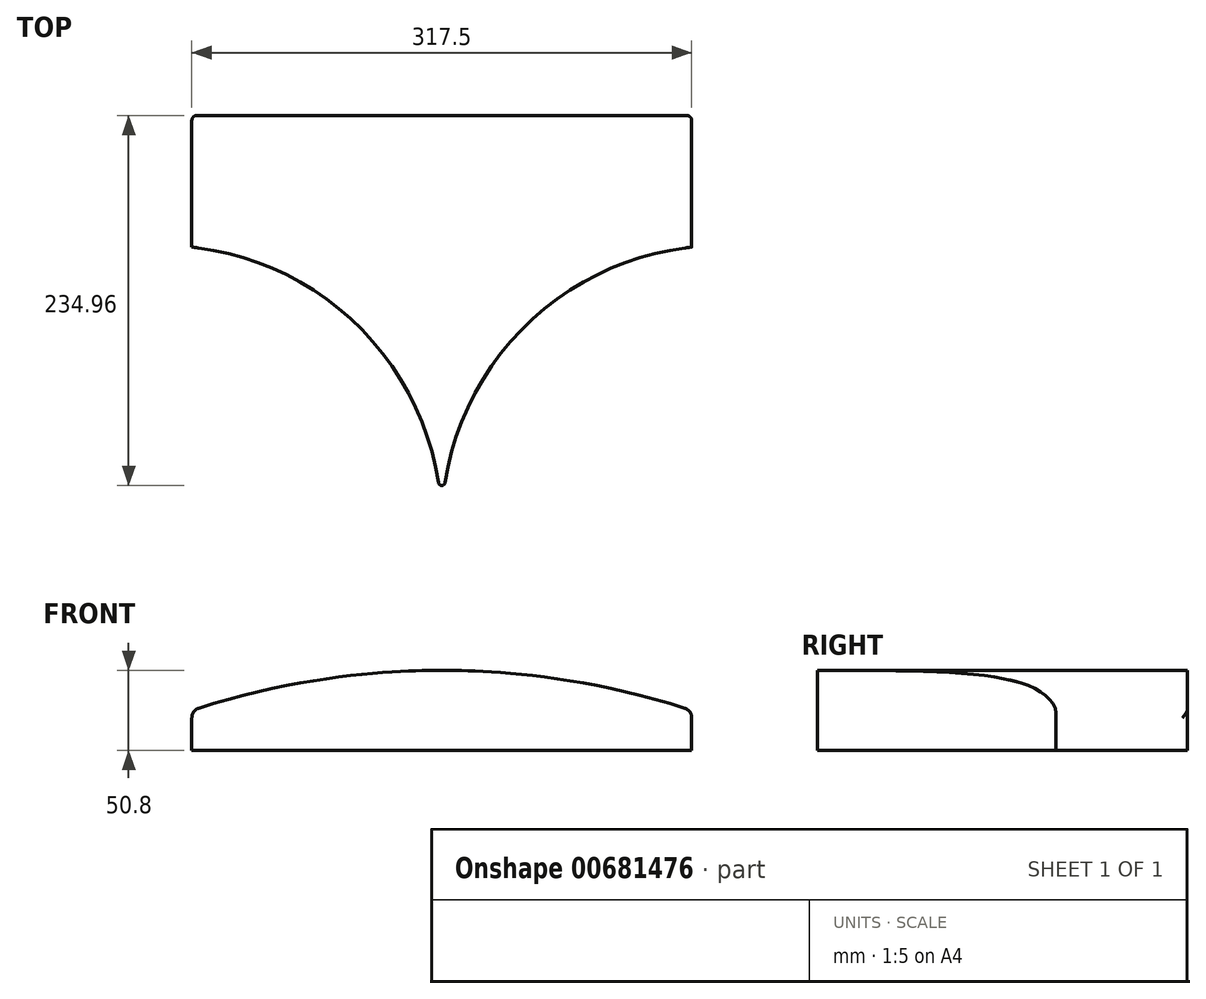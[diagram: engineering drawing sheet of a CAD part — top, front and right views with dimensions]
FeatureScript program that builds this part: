
annotation { "Feature Type Name" : "Feature", "Feature Type Description" : "" }
export const myFeature = defineFeature(function(context is Context, id is Id, definition is map)
    precondition{}
    {
        {
            var Q0;
            Q0=qCreatedBy(makeId("Top.planeOp"),FACE);
            var sketch = newSketch(context, id + "F0", { "sketchPlane" : qUnion([Q0])});
            skLineSegment(sketch, "E0", {"start": v(-155.58, 117.48) * mm, "end": v(155.58, 117.48) * mm});
            skLineSegment(sketch, "E1", {"start": v(158.75, 114.3) * mm, "end": v(158.75, 33.9) * mm});
            skLineSegment(sketch, "E2", {"start": v(-158.75, 114.3) * mm, "end": v(-158.75, 33.9) * mm});
            skArc(sketch, "E3", {"start": v(158.75, 33.9) * mm, "mid": v(55.01, -14.28) * mm, "end": v(2.1, -115.68) * mm});
            skArc(sketch, "E4", {"start": v(-2.1, -115.68) * mm, "mid": v(-55.01, -14.28) * mm, "end": v(-158.75, 33.9) * mm});
            skPoint(sketch, "E5.orphan", {"position": v(-158.75, -29.42) * mm});
            skPoint(sketch, "E6.orphan", {"position": v(158.75, -29.42) * mm});
            skPoint(sketch, "E7.visualSharp", {"position": v(-158.75, 117.48) * mm});
            skArc(sketch, "E7.filletArc", {"start": v(-155.58, 117.48) * mm, "mid": v(-157.82, 116.55) * mm, "end": v(-158.75, 114.3) * mm});
            skPoint(sketch, "E8.visualSharp", {"position": v(158.75, 117.48) * mm});
            skArc(sketch, "E8.filletArc", {"start": v(158.75, 114.3) * mm, "mid": v(157.82, 116.55) * mm, "end": v(155.58, 117.48) * mm});
            skArc(sketch, "E9", {"start": v(-2.1, -115.68) * mm, "mid": v(0, -117.48) * mm, "end": v(2.1, -115.68) * mm});
            skSolve(sketch);
        }
        {
            var Q0;
            Q0 = qSketchRegion(id + "F0", true);
            extrude(context, id + "F1", {"entities" : qUnion([Q0]), "oppositeDirection" : true, "depth" : 50.8 * mm, "offsetDistance" : 25.4 * mm});
        }
        {
            var Q0;
            Q0=qCreatedBy(makeId("Front.planeOp"),FACE);
            var sketch = newSketch(context, id + "F2", { "sketchPlane" : qUnion([Q0])});
            skLineSegment(sketch, "E10", {"start": v(-158.75, -50.8) * mm, "end": v(158.75, -50.8) * mm});
            skArc(sketch, "E11", {"start": v(154.33, -24) * mm, "mid": v(0, 0) * mm, "end": v(-154.33, -24) * mm});
            skLineSegment(sketch, "E12", {"start": v(-158.75, -50.8) * mm, "end": v(-158.75, -30.06) * mm});
            skLineSegment(sketch, "E13", {"start": v(158.75, -50.8) * mm, "end": v(158.75, -30.06) * mm});
            skLineSegment(sketch, "E14.bottom", {"start": v(171.45, -63.5) * mm, "end": v(-171.45, -63.5) * mm});
            skLineSegment(sketch, "E14.top", {"start": v(171.45, 12.7) * mm, "end": v(-171.45, 12.7) * mm});
            skLineSegment(sketch, "E14.left", {"start": v(171.45, -63.5) * mm, "end": v(171.45, 12.7) * mm});
            skLineSegment(sketch, "E14.right", {"start": v(-171.45, -63.5) * mm, "end": v(-171.45, 12.7) * mm});
            skPoint(sketch, "E15.visualSharp", {"position": v(-158.75, -25.44) * mm});
            skArc(sketch, "E15.filletArc", {"start": v(-154.33, -24) * mm, "mid": v(-157.53, -26.31) * mm, "end": v(-158.75, -30.06) * mm});
            skPoint(sketch, "E16.visualSharp", {"position": v(158.75, -25.44) * mm});
            skArc(sketch, "E16.filletArc", {"start": v(158.75, -30.06) * mm, "mid": v(157.53, -26.31) * mm, "end": v(154.33, -24) * mm});
            skSolve(sketch);
        }
        {
            var Q0;
            Q0 = qSketchRegion(id + "F2", true);
            extrude(context, id + "F3", {"entities" : qUnion([Q0]), "operationType" : NewBodyOperationType.REMOVE, "endBound" : BoundingType.SYMMETRIC, "oppositeDirection" : true, "depth" : 254 * mm, "offsetDistance" : 25.4 * mm});
        }
    });
